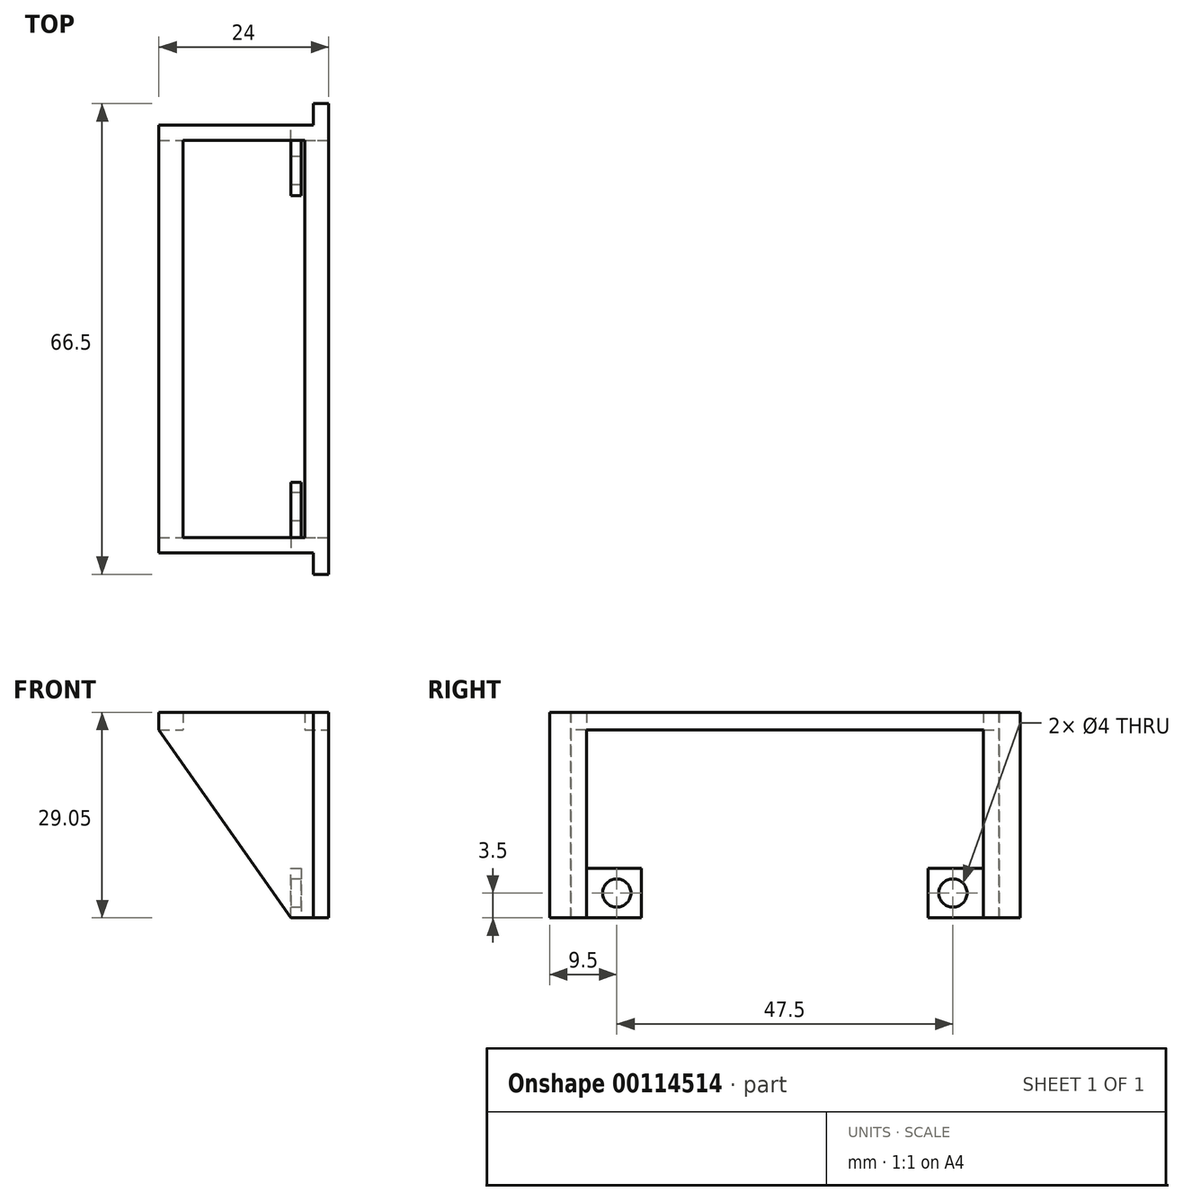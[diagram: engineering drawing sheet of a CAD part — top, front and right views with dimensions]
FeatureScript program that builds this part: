
annotation { "Feature Type Name" : "Feature", "Feature Type Description" : "" }
export const myFeature = defineFeature(function(context is Context, id is Id, definition is map)
    precondition{}
    {
        {
            var Q0;
            Q0=qCreatedBy(makeId("Top.planeOp"),FACE);
            var sketch = newSketch(context, id + "F0", { "sketchPlane" : qUnion([Q0])});
            skLineSegment(sketch, "E0.bottom", {"start": v(-7.9, 27.25) * mm, "end": v(9.35, 27.25) * mm});
            skLineSegment(sketch, "E0.left", {"start": v(-7.9, 27.25) * mm, "end": v(-7.9, 0) * mm});
            skLineSegment(sketch, "E0.right", {"start": v(9.35, 27.25) * mm, "end": v(9.35, 0) * mm});
            skLineSegment(sketch, "E1.bottom", {"start": v(-11.27, 33.25) * mm, "end": v(12.73, 33.25) * mm});
            skLineSegment(sketch, "E1.left", {"start": v(-11.27, 33.25) * mm, "end": v(-11.27, 0) * mm});
            skLineSegment(sketch, "E1.right", {"start": v(12.73, 33.25) * mm, "end": v(12.73, 0) * mm});
            skLineSegment(sketch, "E2", {"start": v(-11.27, 0) * mm, "end": v(12.73, 0) * mm});
            skSolve(sketch);
        }
        {
            var Q0;
            Q0=makeQuery(id+"F0.imprint","IMPRINT",FACE,{"disambiguationData":[TD([[makeQuery(id+"F0.imprint","IMPRINT",EDGE,{"derivedFrom":sQuery(id+"F0.wireOp",EDGE,"E0.bottom")}),1.0]])]});
            extrude(context, id + "F1", {"entities" : qUnion([Q0]), "depth" : 2.5 * mm});
        }
        {
            var Q0;
            Q0=makeQuery(id+"F1.opExtrude","CAP_FACE",FACE,{"disambiguationData":[OSD([sQuery(id+"F0.wireOp",EDGE,"E0.bottom"),sQuery(id+"F0.wireOp",EDGE,"E0.top"),sQuery(id+"F0.wireOp",EDGE,"E0.left"),sQuery(id+"F0.wireOp",EDGE,"E0.right"),sQuery(id+"F0.wireOp",EDGE,"E1.bottom"),sQuery(id+"F0.wireOp",EDGE,"E1.top"),sQuery(id+"F0.wireOp",EDGE,"E1.left"),sQuery(id+"F0.wireOp",EDGE,"E1.right")])],"isStart":true});
            var sketch = newSketch(context, id + "F2", { "sketchPlane" : qUnion([Q0])});
            skLineSegment(sketch, "E3.0", {"start": v(-11.27, -33.25) * mm, "end": v(-11.27, -33.25) * mm});
            skLineSegment(sketch, "E4.0", {"start": v(-11.27, -33.25) * mm, "end": v(12.73, -33.25) * mm});
            skLineSegment(sketch, "E5.0", {"start": v(12.73, -33.25) * mm, "end": v(12.73, -33.25) * mm});
            skLineSegment(sketch, "E6.0", {"start": v(-11.27, -27.25) * mm, "end": v(12.73, -27.25) * mm});
            skLineSegment(sketch, "E7.0", {"start": v(-11.27, -33.25) * mm, "end": v(-11.27, 0) * mm});
            skLineSegment(sketch, "E8.0", {"start": v(12.73, -33.25) * mm, "end": v(12.73, 0) * mm});
            skPoint(sketch, "E9.orphan", {"position": v(-7.9, -27.25) * mm});
            skPoint(sketch, "E10.orphan", {"position": v(9.35, -27.25) * mm});
            skSolve(sketch);
        }
        {
            var Q0;
            {var subQ7=sQuery(id+"F2.wireOp",EDGE,"E4.0");Q0=makeQuery(id+"F2.imprint","IMPRINT",FACE,{"disambiguationData":[TD([[makeQuery(id+"F2.imprint","IMPRINT",EDGE,{"derivedFrom":subQ7}),1.0]])]});}
            extrude(context, id + "F3", {"entities" : qUnion([Q0]), "operationType" : NewBodyOperationType.ADD, "depth" : 26.55 * mm});
        }
        {
            var Q0;
            Q0=makeQuery(id+"F3.boolean.opBoolean","MERGE",FACE,{"derivedFrom":[makeQuery(id+"F1.opExtrude","SWEPT_FACE",FACE,{"disambiguationData":[OSD([sQuery(id+"F0.wireOp",EDGE,"E1.bottom")])]}),makeQuery(id+"F3.opExtrude","SWEPT_FACE",FACE,{"disambiguationData":[OSD([sQuery(id+"F2.wireOp",EDGE,"E4.0")])]})]});
            var sketch = newSketch(context, id + "F4", { "sketchPlane" : qUnion([Q0])});
            skLineSegment(sketch, "E11.0", {"start": v(11.27, 0) * mm, "end": v(-12.73, 0) * mm});
            skLineSegment(sketch, "E12.0", {"start": v(11.27, 2.5) * mm, "end": v(11.27, -26.55) * mm});
            skLineSegment(sketch, "E13.0", {"start": v(-12.73, 2.5) * mm, "end": v(-12.73, -26.55) * mm});
            skLineSegment(sketch, "E14", {"start": v(11.27, 0) * mm, "end": v(-7.35, -26.55) * mm});
            skLineSegment(sketch, "E15.0", {"start": v(-9.35, 2.5) * mm, "end": v(-9.35, -26.55) * mm, "construction": true});
            skPoint(sketch, "E16.orphan", {"position": v(-9.35, 0) * mm});
            skLineSegment(sketch, "E17.1", {"start": v(11.27, -26.55) * mm, "end": v(-12.73, -26.55) * mm});
            skSolve(sketch);
        }
        {
            var Q0;
            {var subQ3=sQuery(id+"F4.wireOp",EDGE,"E14");Q0=makeQuery(id+"F4.imprint","IMPRINT",FACE,{"disambiguationData":[TD([[makeQuery(id+"F4.imprint","IMPRINT",EDGE,{"derivedFrom":subQ3}),1.0]])]});}
            extrude(context, id + "F5", {"entities" : qUnion([Q0]), "operationType" : NewBodyOperationType.REMOVE, "endBound" : BoundingType.THROUGH_ALL, "oppositeDirection" : true, "depth" : 25 * mm});
        }
        {
            var Q0;
            Q0=makeQuery(id+"F3.boolean.opBoolean","MERGE",FACE,{"derivedFrom":[makeQuery(id+"F1.opExtrude","SWEPT_FACE",FACE,{"disambiguationData":[OSD([sQuery(id+"F0.wireOp",EDGE,"E0.bottom")])]}),makeQuery(id+"F3.opExtrude","SWEPT_FACE",FACE,{"disambiguationData":[OSD([sQuery(id+"F2.wireOp",EDGE,"E6.0")])]})]});
            var sketch = newSketch(context, id + "F6", { "sketchPlane" : qUnion([Q0])});
            skLineSegment(sketch, "E18", {"start": v(7.35, -26.55) * mm, "end": v(7.35, -19.55) * mm});
            skLineSegment(sketch, "E19", {"start": v(7.35, -19.55) * mm, "end": v(8.85, -19.55) * mm});
            skLineSegment(sketch, "E20", {"start": v(8.85, -19.55) * mm, "end": v(8.85, -26.55) * mm});
            skLineSegment(sketch, "E21.0", {"start": v(7.35, -26.55) * mm, "end": v(12.73, -26.55) * mm});
            skLineSegment(sketch, "E22.0", {"start": v(9.35, 0) * mm, "end": v(9.35, -26.55) * mm, "construction": true});
            skPoint(sketch, "E23.orphan", {"position": v(9.35, 2.5) * mm});
            skSolve(sketch);
        }
        {
            var Q0;
            {var subQ0=sQuery(id+"F6.wireOp",EDGE,"E18");Q0=makeQuery(id+"F6.imprint","IMPRINT",FACE,{"disambiguationData":[TD([[makeQuery(id+"F6.imprint","IMPRINT",EDGE,{"derivedFrom":subQ0}),-1.0]])]});}
            extrude(context, id + "F7", {"entities" : qUnion([Q0]), "operationType" : NewBodyOperationType.ADD, "depth" : 7 * mm});
        }
        {
            var Q0;
            Q0=makeQuery(id+"F7.opExtrude","SWEPT_FACE",FACE,{"disambiguationData":[OSD([sQuery(id+"F6.wireOp",EDGE,"E18")])]});
            var sketch = newSketch(context, id + "F8", { "sketchPlane" : qUnion([Q0])});
            skLineSegment(sketch, "E24", {"start": v(-23.75, -19.55) * mm, "end": v(-23.75, -26.55) * mm, "construction": true});
            skCircle(sketch, "E25", {"center": v(-23.75, -23.05) * mm, "radius": 2 * mm});
            skSolve(sketch);
        }
        {
            var Q0;
            Q0=makeQuery(id+"F8.imprint","IMPRINT",FACE,{"disambiguationData":[TD([[makeQuery(id+"F8.imprint","IMPRINT",EDGE,{"derivedFrom":sQuery(id+"F8.wireOp",EDGE,"E25")}),1.0]])]});
            extrude(context, id + "F9", {"entities" : qUnion([Q0]), "operationType" : NewBodyOperationType.REMOVE, "oppositeDirection" : true, "depth" : 25 * mm});
        }
        {
            var Q0;
            Q0=makeQuery(id+"F3.boolean.opBoolean","MERGE",FACE,{"derivedFrom":[makeQuery(id+"F1.opExtrude","SWEPT_FACE",FACE,{"disambiguationData":[OSD([sQuery(id+"F0.wireOp",EDGE,"E1.bottom")])]}),makeQuery(id+"F3.opExtrude","SWEPT_FACE",FACE,{"disambiguationData":[OSD([sQuery(id+"F2.wireOp",EDGE,"E4.0")])]})]});
            var sketch = newSketch(context, id + "F10", { "sketchPlane" : qUnion([Q0])});
            skPoint(sketch, "E26.0", {"position": v(11.27, 0) * mm});
            skLineSegment(sketch, "E27.0", {"start": v(11.27, 0) * mm, "end": v(-7.35, -26.55) * mm});
            skLineSegment(sketch, "E28.0", {"start": v(-12.73, 2.5) * mm, "end": v(-12.73, -26.55) * mm});
            skLineSegment(sketch, "E29.0", {"start": v(11.27, 2.5) * mm, "end": v(-12.73, 2.5) * mm});
            skLineSegment(sketch, "E30.0", {"start": v(11.27, 2.5) * mm, "end": v(11.27, 0) * mm});
            skLineSegment(sketch, "E31.0", {"start": v(-7.35, -26.55) * mm, "end": v(-12.73, -26.55) * mm});
            skLineSegment(sketch, "E32", {"start": v(-10.58, -26.55) * mm, "end": v(-10.58, 2.5) * mm});
            skSolve(sketch);
        }
        {
            var Q0;
            {var subQ1=sQuery(id+"F10.wireOp",EDGE,"E27.0");Q0=makeQuery(id+"F10.imprint","IMPRINT",FACE,{"disambiguationData":[TD([[makeQuery(id+"F10.imprint","IMPRINT",EDGE,{"derivedFrom":subQ1}),-1.0]])]});}
            extrude(context, id + "F11", {"entities" : qUnion([Q0]), "operationType" : NewBodyOperationType.REMOVE, "oppositeDirection" : true, "depth" : 3 * mm});
        }
        {
            var Q0;
            Q0=makeQuery(id+"F6.imprint","IMPRINT",FACE,{"disambiguationData":[TD([[makeQuery(id+"F6.imprint","IMPRINT",EDGE,{"derivedFrom":sQuery(id+"F6.wireOp",EDGE,"E18")}),1.0]])]});
            extrude(context, id + "F12", {"entities" : qUnion([Q0]), "operationType" : NewBodyOperationType.REMOVE, "oppositeDirection" : true, "depth" : .80 * mm});
        }
        {
            var Q0;
            Q0=makeQuery(id+"F1.opExtrude","SWEPT_BODY",BODY,{"disambiguationData":[OSD([sQuery(id+"F0.wireOp",EDGE,"E0.bottom"),sQuery(id+"F0.wireOp",EDGE,"E0.left"),sQuery(id+"F0.wireOp",EDGE,"E0.right"),sQuery(id+"F0.wireOp",EDGE,"E1.bottom"),sQuery(id+"F0.wireOp",EDGE,"E1.left"),sQuery(id+"F0.wireOp",EDGE,"E1.right"),sQuery(id+"F0.wireOp",EDGE,"E2")])]});
            var Q1;
            {var subQ0=sQuery(id+"F0.wireOp",EDGE,"E2");Q1=makeQuery(id+"F1.opExtrude","SWEPT_FACE",FACE,{"disambiguationData":[OSD([subQ0]),TDD([makeQuery(id+"F0.imprint","IMPRINT",EDGE,{"disambiguationData":[TD([[makeQuery(id+"F0.imprint","INTERSECT",VERTEX,{"derivedFrom":[sQuery(id+"F0.wireOp",EDGE,"E0.left"),subQ0]}),1.0]])],"derivedFrom":subQ0})])]});}
            mirror(context, id + "F13", {"operationType" : NewBodyOperationType.ADD, "entities" : qUnion([Q0]), "mirrorPlane" : qUnion([Q1])});
        }
    });
